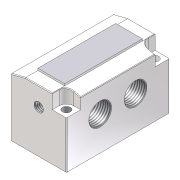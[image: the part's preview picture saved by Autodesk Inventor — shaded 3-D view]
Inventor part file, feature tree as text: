
AUTODESK INVENTOR PART (.ipt)
format: ipt  version: unknown  size: 286,720 bytes
history: native  units: in
note: dims shown in document units (in); Inventor stores cm internally (conversion verified against a paired STEP export)
features: sketch x5, hole x4, extrude x3, fillet x2, mirror x2, chamfer x2
ambient origin geometry x8: Origin, YZ Plane, XZ Plane, XY Plane, X Axis, Y Axis, Z Axis, Center Point
feature tree (18):
  extrude  "Extrusion1"  Depth=0.91in
  extrude  "Extrusion2"  Depth=0.42in
  fillet  "Fillet1"  Radius=1.615in
  hole  "Hole1"  [1 undecoded]
  mirror  "Mirror1"
  hole  "Hole2"  [1 undecoded]
  hole  "Hole3"  [1 undecoded]
  chamfer  "Chamfer1"  Distance=0.67in
  mirror  "Mirror2"
  hole  "Hole4"  [1 undecoded]
  chamfer  "Chamfer2"  Distance=0.3in
  fillet  "Fillet2"  Radius=0.38in
  extrude  "Extrusion3"  Depth=0.67in
  sketch  "Sketch1"  dims[d0=0.87in d1=0.91in]
  sketch  "Sketch2"  dims[d2=0.965in d3=0.42in d4=1.615in d5=0.0in]
  sketch  "Sketch3"  dims[d6=0.224in d7=0.225in d8=0.0in]
  sketch  "Sketch4"  dims[d9=0.115in d10=0.115in d11=0.115in]
  sketch  "Sketch5"  dims[d12=0.125in d13=0.5in d14=0.375in d15=0.25in d16=0.5635in d17=0.75in d18=0.8108in d19=0.53in d20=0.53in d21=0.337in d22=0.5in d23=0.375in d24=0.25in d25=0.5635in d26=0.275in d27=0.0in d28=0.67in d29=0.128in d30=0.5in d31=0.375in d32=0.25in d33=0.5635in d34=0.32in d35=0.8108in d36=0.01in d37=0.125in d38=45.0deg d39=0.3in d41=0.38in d42=0.67in d43=0.38in d44=0.337in d45=0.5in d46=0.375in d47=0.25in d48=0.5635in d49=0.28in d50=0.0in d51=0.01in d52=0.125in d53=45.0deg d54=0.01in d55=1.22in d56=0.03in d57=0.0in]
note: 4 required parameter values undecoded (feature->parameter linkage not recoverable at this tier; creation-order binding heuristic only, values carry confidence <= 0.55)
